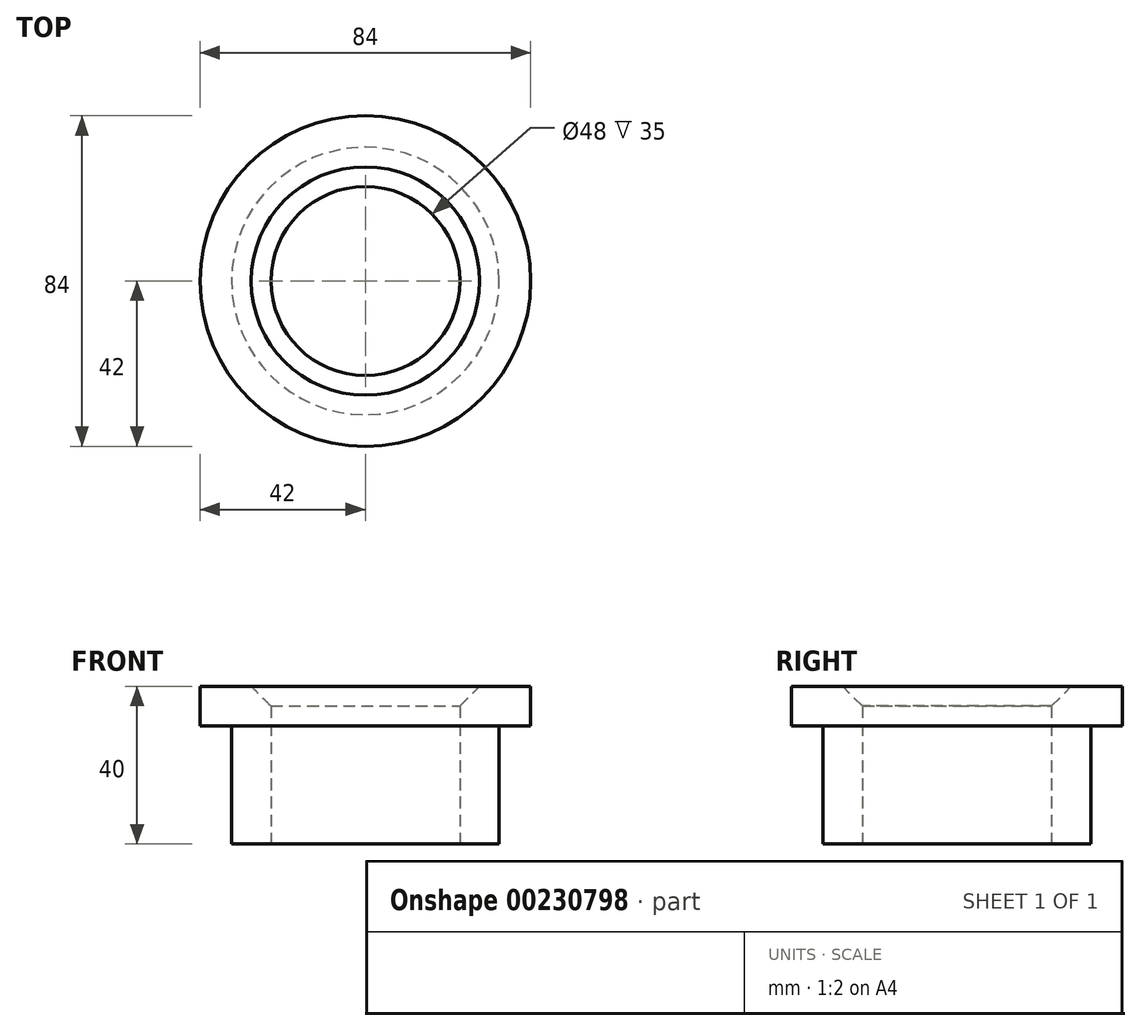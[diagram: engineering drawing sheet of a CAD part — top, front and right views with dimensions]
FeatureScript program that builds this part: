
annotation { "Feature Type Name" : "Feature", "Feature Type Description" : "" }
export const myFeature = defineFeature(function(context is Context, id is Id, definition is map)
    precondition{}
    {
        {
            var Q0;
            Q0=qCreatedBy(makeId("Front.planeOp"),FACE);
            var sketch = newSketch(context, id + "F0", { "sketchPlane" : qUnion([Q0])});
            skLineSegment(sketch, "E0", {"start": v(34, 0) * mm, "end": v(34, 30) * mm});
            skLineSegment(sketch, "E1", {"start": v(34, 30) * mm, "end": v(42, 30) * mm});
            skLineSegment(sketch, "E2", {"start": v(42, 30) * mm, "end": v(42, 40) * mm});
            skLineSegment(sketch, "E3", {"start": v(0, 0) * mm, "end": v(0, 39.5) * mm, "construction": true});
            skLineSegment(sketch, "E4", {"start": v(24, 0) * mm, "end": v(24, 40) * mm});
            skLineSegment(sketch, "E5", {"start": v(24, 40) * mm, "end": v(42, 40) * mm});
            skLineSegment(sketch, "E6", {"start": v(24, 0) * mm, "end": v(34, 0) * mm});
            skSolve(sketch);
        }
        {
            var Q0;
            Q0 = qSketchRegion(id + "F0", true);
            var Q1;
            Q1=sQuery(id+"F0.wireOp",EDGE,"E3");
            revolve(context, id + "F1", {"entities" : qUnion([Q0]), "axis" : qUnion([Q1]), "revolveType" : RevolveType.FULL});
        }
        {
            var Q0;
            Q0=makeQuery(id+"F1.opRevolve","SWEPT_EDGE",EDGE,{"disambiguationData":[OSD([sQuery(id+"F0.wireOp",EDGE,"E4"),sQuery(id+"F0.wireOp",EDGE,"E5")])]});
            chamfer(context, id + "F2", {"entities" : qUnion([Q0]), "width" : 5 * mm, "tangentPropagation" : true});
        }
    });
